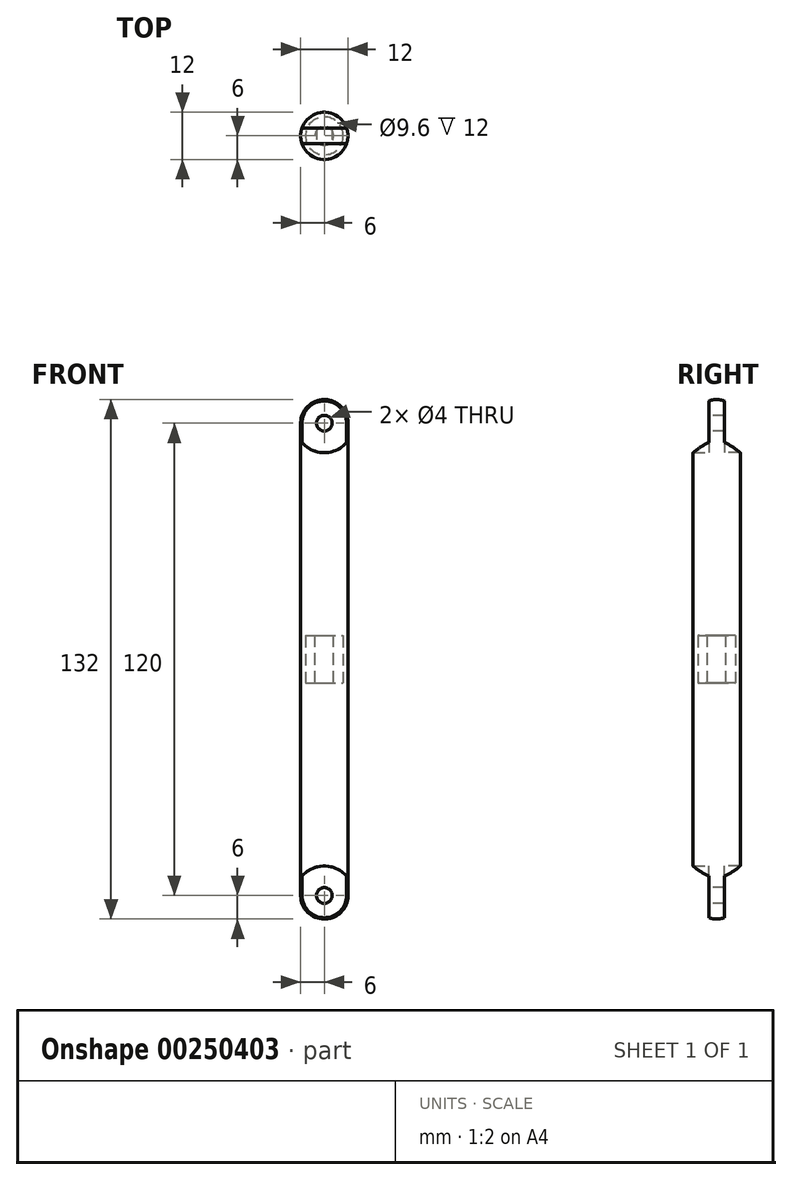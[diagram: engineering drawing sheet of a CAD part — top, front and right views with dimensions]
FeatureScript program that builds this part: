
annotation { "Feature Type Name" : "Feature", "Feature Type Description" : "" }
export const myFeature = defineFeature(function(context is Context, id is Id, definition is map)
    precondition{}
    {
        {
            var Q0;
            Q0=qCreatedBy(makeId("Top.planeOp"),FACE);
            var sketch = newSketch(context, id + "F0", { "sketchPlane" : qUnion([Q0])});
            skCircle(sketch, "E0", {"center": v(0, 0) * mm, "radius": 6 * mm});
            skSolve(sketch);
        }
        {
            var Q0;
            Q0=qSketchRegion(id+"F0",true);
            extrude(context, id + "F1", {"entities" : qUnion([Q0]), "depth" : 66 * mm});
        }
        {
            var Q0;
            Q0=qCreatedBy(makeId("Front.planeOp"),FACE);
            var sketch = newSketch(context, id + "F2", { "sketchPlane" : qUnion([Q0])});
            skArc(sketch, "E1", {"start": v(-6.02, 55.53) * mm, "mid": v(0.12, 52.5) * mm, "end": v(6.16, 55.73) * mm});
            skLineSegment(sketch, "E2", {"start": v(-6.02, 66.02) * mm, "end": v(6.16, 66.02) * mm});
            skLineSegment(sketch, "E3", {"start": v(6.16, 66.02) * mm, "end": v(6.16, 55.73) * mm});
            skLineSegment(sketch, "E4", {"start": v(-6.02, 66.02) * mm, "end": v(-6.02, 55.53) * mm});
            skSolve(sketch);
        }
        {
            var Q0;
            Q0=qSketchRegion(id+"F2",true);
            extrude(context, id + "F3", {"entities" : qUnion([Q0]), "operationType" : NewBodyOperationType.REMOVE, "endBound" : BoundingType.UP_TO_NEXT, "oppositeDirection" : true, "depth" : 6 * mm, "hasSecondDirection" : true, "secondDirectionOppositeDirection" : true, "secondDirectionDepth" : 2 * mm});
        }
        {
            var Q0;
            Q0=qSketchRegion(id+"F2",true);
            extrude(context, id + "F4", {"entities" : qUnion([Q0]), "operationType" : NewBodyOperationType.REMOVE, "depth" : 6 * mm, "hasSecondDirection" : true, "secondDirectionOppositeDirection" : false, "secondDirectionDepth" : 2 * mm});
        }
        {
            var Q0;
            Q0=makeQuery(id+"F4.boolean.opBoolean","SPLIT",EDGE,{"disambiguationData":[OD(1.0)],"derivedFrom":makeQuery(id+"F1.opExtrude","CAP_EDGE",EDGE,{"disambiguationData":[OSD([sQuery(id+"F0.wireOp",EDGE,"E0")])],"isStart":false})});
            fillet(context, id + "F5", {"entities" : qUnion([Q0]), "radius" : 6 * mm, "tangentPropagation" : true, "allowEdgeOverflow" : false});
        }
        {
            var Q0;
            Q0=makeQuery(id+"F2.imprint","IMPRINT",FACE,{"disambiguationData":[TD([[makeQuery(id+"F2.imprint","IMPRINT",EDGE,{"derivedFrom":sQuery(id+"F2.wireOp",EDGE,"E1")}),1.0]])]});
            var sketch = newSketch(context, id + "F6", { "sketchPlane" : qUnion([Q0])});
            skCircle(sketch, "E5", {"center": v(0, 60) * mm, "radius": 2 * mm});
            skSolve(sketch);
        }
        {
            var Q0;
            Q0=qSketchRegion(id+"F6",true);
            extrude(context, id + "F7", {"entities" : qUnion([Q0]), "operationType" : NewBodyOperationType.REMOVE, "endBound" : BoundingType.SYMMETRIC, "oppositeDirection" : true, "depth" : 25 * mm});
        }
        {
            var Q0;
            Q0=makeQuery(id+"F1.opExtrude","CAP_FACE",FACE,{"disambiguationData":[OSD([sQuery(id+"F0.wireOp",EDGE,"E0")])],"isStart":true});
            var sketch = newSketch(context, id + "F8", { "sketchPlane" : qUnion([Q0])});
            skCircle(sketch, "E6", {"center": v(0, 0) * mm, "radius": 4.8 * mm});
            skSolve(sketch);
        }
        {
            var Q0;
            Q0=qSketchRegion(id+"F8",true);
            extrude(context, id + "F9", {"entities" : qUnion([Q0]), "operationType" : NewBodyOperationType.REMOVE, "oppositeDirection" : true, "depth" : 6 * mm});
        }
        {
            var Q0;
            Q0=makeQuery(id+"F9.boolean.opBoolean","COPY",FACE,{"derivedFrom":makeQuery(id+"F9.opExtrude","CAP_FACE",FACE,{"disambiguationData":[OSD([sQuery(id+"F8.wireOp",EDGE,"E6")])],"isStart":false})});
            var sketch = newSketch(context, id + "F10", { "sketchPlane" : qUnion([Q0])});
            skCircle(sketch, "E7", {"center": v(0, 0) * mm, "radius": 2.37 * mm});
            skSolve(sketch);
        }
        {
            var Q0;
            Q0=qSketchRegion(id+"F10",true);
            extrude(context, id + "F11", {"entities" : qUnion([Q0]), "operationType" : NewBodyOperationType.ADD, "depth" : 7.5 * mm});
        }
        {
            var Q0;
            Q0=makeQuery(id+"F1.opExtrude","SWEPT_BODY",BODY,{"disambiguationData":[OSD([sQuery(id+"F0.wireOp",EDGE,"E0")])]});
            var Q1;
            Q1=qCreatedBy(makeId("Top.planeOp"),FACE);
            mirror(context, id + "F12", {"operationType" : NewBodyOperationType.ADD, "entities" : qUnion([Q0]), "mirrorPlane" : qUnion([Q1])});
        }
    });
